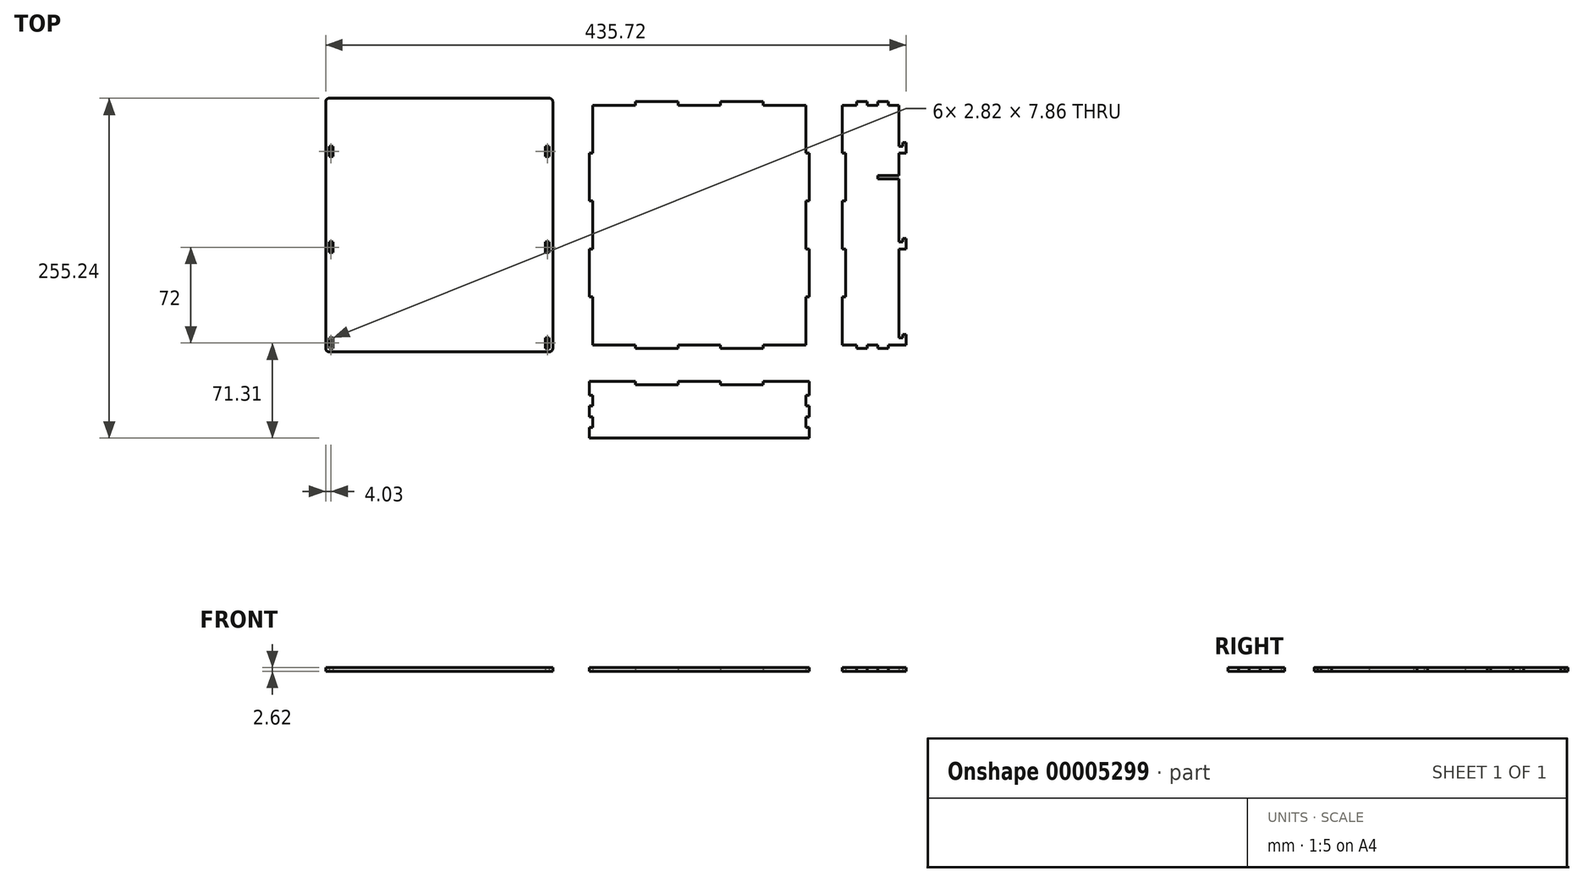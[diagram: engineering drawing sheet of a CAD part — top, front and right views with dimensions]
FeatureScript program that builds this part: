
annotation { "Feature Type Name" : "Feature", "Feature Type Description" : "" }
export const myFeature = defineFeature(function(context is Context, id is Id, definition is map)
    precondition{}
    {
        {
            assignVariable(context, id + "F0", {"name" : "MaterialThickness", "anyValue" : 2.62});
        }
        {
            var Q0;
            Q0=qCreatedBy(makeId("Top.planeOp"),FACE);
            var sketch = newSketch(context, id + "F1", { "sketchPlane" : qUnion([Q0])});
            skLineSegment(sketch, "E0", {"start": v(0, 0) * mm, "end": v(160, 0) * mm});
            skLineSegment(sketch, "E1", {"start": v(160, 0) * mm, "end": v(160, 180) * mm});
            skLineSegment(sketch, "E2", {"start": v(160, 180) * mm, "end": v(0, 180) * mm});
            skLineSegment(sketch, "E3", {"start": v(0, 180) * mm, "end": v(0, 0) * mm});
            skLineSegment(sketch, "E4", {"start": v(64, 182.62) * mm, "end": v(64, 180) * mm});
            skLineSegment(sketch, "E5", {"start": v(96, 180) * mm, "end": v(96, 182.62) * mm});
            skLineSegment(sketch, "E6", {"start": v(96, 182.62) * mm, "end": v(128, 182.62) * mm});
            skLineSegment(sketch, "E7", {"start": v(128, 182.62) * mm, "end": v(128, 180) * mm});
            skLineSegment(sketch, "E8", {"start": v(64, 182.62) * mm, "end": v(32, 182.62) * mm});
            skLineSegment(sketch, "E9", {"start": v(32, 182.62) * mm, "end": v(32, 180) * mm});
            skLineSegment(sketch, "E10", {"start": v(0, 90) * mm, "end": v(160, 90) * mm, "construction": true});
            skLineSegment(sketch, "E11.MirrorCS", {"start": v(64, -2.62) * mm, "end": v(64, 0) * mm});
            skLineSegment(sketch, "E12.MirrorCS", {"start": v(128, -2.62) * mm, "end": v(128, 0) * mm});
            skLineSegment(sketch, "E13.MirrorCS", {"start": v(32, -2.62) * mm, "end": v(32, 0) * mm});
            skLineSegment(sketch, "E14.MirrorCS", {"start": v(64, -2.62) * mm, "end": v(32, -2.62) * mm});
            skLineSegment(sketch, "E15.MirrorCS", {"start": v(96, 0) * mm, "end": v(96, -2.62) * mm});
            skLineSegment(sketch, "E16.MirrorCS", {"start": v(96, -2.62) * mm, "end": v(128, -2.62) * mm});
            skLineSegment(sketch, "E17", {"start": v(0, 144) * mm, "end": v(-2.62, 144) * mm});
            skLineSegment(sketch, "E18", {"start": v(-2.62, 144) * mm, "end": v(-2.62, 108) * mm});
            skLineSegment(sketch, "E19", {"start": v(-2.62, 108) * mm, "end": v(0, 108) * mm});
            skLineSegment(sketch, "E20", {"start": v(0, 72) * mm, "end": v(-2.62, 72) * mm});
            skLineSegment(sketch, "E21", {"start": v(-2.62, 72) * mm, "end": v(-2.62, 36) * mm});
            skLineSegment(sketch, "E22", {"start": v(-2.62, 36) * mm, "end": v(0, 36) * mm});
            skLineSegment(sketch, "E23", {"start": v(80, 180) * mm, "end": v(80, 0) * mm, "construction": true});
            skLineSegment(sketch, "E24.MirrorCS", {"start": v(162.62, 144) * mm, "end": v(162.62, 108) * mm});
            skLineSegment(sketch, "E25.MirrorCS", {"start": v(162.62, 108) * mm, "end": v(160, 108) * mm});
            skLineSegment(sketch, "E26.MirrorCS", {"start": v(162.62, 36) * mm, "end": v(160, 36) * mm});
            skLineSegment(sketch, "E27.MirrorCS", {"start": v(162.62, 72) * mm, "end": v(162.62, 36) * mm});
            skLineSegment(sketch, "E28.MirrorCS", {"start": v(160, 144) * mm, "end": v(162.62, 144) * mm});
            skLineSegment(sketch, "E29.MirrorCS", {"start": v(160, 72) * mm, "end": v(162.62, 72) * mm});
            skLineSegment(sketch, "E30", {"start": v(0, -30) * mm, "end": v(160, -30) * mm});
            skLineSegment(sketch, "E31", {"start": v(160, -30) * mm, "end": v(160, -70) * mm});
            skLineSegment(sketch, "E32", {"start": v(160, -70) * mm, "end": v(0, -70) * mm});
            skLineSegment(sketch, "E33", {"start": v(0, -70) * mm, "end": v(0, -30) * mm});
            skLineSegment(sketch, "E34", {"start": v(0, -30) * mm, "end": v(0, -27.38) * mm});
            skLineSegment(sketch, "E35", {"start": v(0, -27.38) * mm, "end": v(32, -27.38) * mm});
            skLineSegment(sketch, "E36", {"start": v(32, -27.38) * mm, "end": v(32, -30) * mm});
            skLineSegment(sketch, "E37", {"start": v(64, -30) * mm, "end": v(64, -27.38) * mm});
            skLineSegment(sketch, "E38", {"start": v(64, -27.38) * mm, "end": v(96, -27.38) * mm});
            skLineSegment(sketch, "E39", {"start": v(96, -27.38) * mm, "end": v(96, -30) * mm});
            skLineSegment(sketch, "E40", {"start": v(128, -30) * mm, "end": v(128, -27.38) * mm});
            skLineSegment(sketch, "E41", {"start": v(128, -27.38) * mm, "end": v(160, -27.38) * mm});
            skLineSegment(sketch, "E42", {"start": v(160, -27.38) * mm, "end": v(160, -30) * mm});
            skLineSegment(sketch, "E43", {"start": v(0, -27.38) * mm, "end": v(-2.62, -27.38) * mm});
            skLineSegment(sketch, "E44", {"start": v(-2.62, -27.38) * mm, "end": v(-2.62, -38) * mm});
            skLineSegment(sketch, "E45", {"start": v(-2.62, -38) * mm, "end": v(0, -38) * mm});
            skLineSegment(sketch, "E46", {"start": v(0, -46) * mm, "end": v(-2.62, -46) * mm});
            skLineSegment(sketch, "E47", {"start": v(-2.62, -46) * mm, "end": v(-2.62, -54) * mm});
            skLineSegment(sketch, "E48", {"start": v(-2.62, -54) * mm, "end": v(0, -54) * mm});
            skLineSegment(sketch, "E49", {"start": v(0, -70) * mm, "end": v(-2.62, -70) * mm});
            skLineSegment(sketch, "E50", {"start": v(-2.62, -70) * mm, "end": v(-2.62, -62) * mm});
            skLineSegment(sketch, "E51", {"start": v(-2.62, -62) * mm, "end": v(0, -62) * mm});
            skLineSegment(sketch, "E52", {"start": v(80, -30) * mm, "end": v(80, -70) * mm, "construction": true});
            skLineSegment(sketch, "E53.MirrorCS", {"start": v(160, -27.38) * mm, "end": v(162.62, -27.38) * mm});
            skLineSegment(sketch, "E54.MirrorCS", {"start": v(160, -70) * mm, "end": v(162.62, -70) * mm});
            skLineSegment(sketch, "E55.MirrorCS", {"start": v(160, -46) * mm, "end": v(162.62, -46) * mm});
            skLineSegment(sketch, "E56.MirrorCS", {"start": v(162.62, -38) * mm, "end": v(160, -38) * mm});
            skLineSegment(sketch, "E57.MirrorCS", {"start": v(162.62, -54) * mm, "end": v(160, -54) * mm});
            skLineSegment(sketch, "E58.MirrorCS", {"start": v(162.62, -62) * mm, "end": v(160, -62) * mm});
            skLineSegment(sketch, "E59.MirrorCS", {"start": v(162.62, -27.38) * mm, "end": v(162.62, -38) * mm});
            skLineSegment(sketch, "E60.MirrorCS", {"start": v(162.62, -46) * mm, "end": v(162.62, -54) * mm});
            skLineSegment(sketch, "E61.MirrorCS", {"start": v(162.62, -70) * mm, "end": v(162.62, -62) * mm});
            skLineSegment(sketch, "E62", {"start": v(190, 0) * mm, "end": v(190, 180) * mm});
            skLineSegment(sketch, "E63", {"start": v(190, 180) * mm, "end": v(230, 180) * mm});
            skLineSegment(sketch, "E64", {"start": v(230, 180) * mm, "end": v(230, 0) * mm});
            skLineSegment(sketch, "E65", {"start": v(230, 0) * mm, "end": v(190, 0) * mm});
            skLineSegment(sketch, "E66", {"start": v(198, 0) * mm, "end": v(198, -2.62) * mm});
            skLineSegment(sketch, "E67", {"start": v(198, -2.62) * mm, "end": v(206, -2.62) * mm});
            skLineSegment(sketch, "E68", {"start": v(206, -2.62) * mm, "end": v(206, 0) * mm});
            skLineSegment(sketch, "E69", {"start": v(214, 0) * mm, "end": v(214, -2.62) * mm});
            skLineSegment(sketch, "E70", {"start": v(214, -2.62) * mm, "end": v(222, -2.62) * mm});
            skLineSegment(sketch, "E71", {"start": v(222, -2.62) * mm, "end": v(222, 0) * mm});
            skLineSegment(sketch, "E72", {"start": v(190, 0) * mm, "end": v(187.38, 0) * mm});
            skLineSegment(sketch, "E73", {"start": v(187.38, 0) * mm, "end": v(187.38, 36) * mm});
            skLineSegment(sketch, "E74", {"start": v(187.38, 36) * mm, "end": v(190, 36) * mm});
            skLineSegment(sketch, "E75", {"start": v(190, 72) * mm, "end": v(187.38, 72) * mm});
            skLineSegment(sketch, "E76", {"start": v(187.38, 72) * mm, "end": v(187.38, 108) * mm});
            skLineSegment(sketch, "E77", {"start": v(187.38, 108) * mm, "end": v(190, 108) * mm});
            skLineSegment(sketch, "E78", {"start": v(190, 144) * mm, "end": v(187.38, 144) * mm});
            skLineSegment(sketch, "E79", {"start": v(187.38, 144) * mm, "end": v(187.38, 180) * mm});
            skLineSegment(sketch, "E80", {"start": v(187.38, 180) * mm, "end": v(190, 180) * mm});
            skLineSegment(sketch, "E81", {"start": v(190, 90) * mm, "end": v(230, 90) * mm, "construction": true});
            skLineSegment(sketch, "E82.MirrorCS", {"start": v(214, 180) * mm, "end": v(214, 182.62) * mm});
            skLineSegment(sketch, "E83.MirrorCS", {"start": v(222, 182.62) * mm, "end": v(222, 180) * mm});
            skLineSegment(sketch, "E84.MirrorCS", {"start": v(206, 182.62) * mm, "end": v(206, 180) * mm});
            skLineSegment(sketch, "E85.MirrorCS", {"start": v(198, 180) * mm, "end": v(198, 182.62) * mm});
            skLineSegment(sketch, "E86.MirrorCS", {"start": v(198, 182.62) * mm, "end": v(206, 182.62) * mm});
            skLineSegment(sketch, "E87.MirrorCS", {"start": v(214, 182.62) * mm, "end": v(222, 182.62) * mm});
            skLineSegment(sketch, "E88", {"start": v(230, 0) * mm, "end": v(235.24, 0) * mm});
            skLineSegment(sketch, "E89", {"start": v(235.24, 0) * mm, "end": v(235.24, 7.86) * mm});
            skLineSegment(sketch, "E90", {"start": v(235.24, 7.86) * mm, "end": v(232.62, 7.86) * mm});
            skLineSegment(sketch, "E91", {"start": v(232.62, 7.86) * mm, "end": v(232.62, 5.24) * mm});
            skLineSegment(sketch, "E92", {"start": v(232.62, 5.24) * mm, "end": v(230, 5.24) * mm});
            skLineSegment(sketch, "E93", {"start": v(230, 72) * mm, "end": v(235.24, 72) * mm});
            skLineSegment(sketch, "E94", {"start": v(235.24, 72) * mm, "end": v(235.24, 79.86) * mm});
            skLineSegment(sketch, "E95", {"start": v(235.24, 79.86) * mm, "end": v(232.62, 79.86) * mm});
            skLineSegment(sketch, "E96", {"start": v(232.62, 79.86) * mm, "end": v(232.62, 77.24) * mm});
            skLineSegment(sketch, "E97", {"start": v(232.62, 77.24) * mm, "end": v(230, 77.24) * mm});
            skLineSegment(sketch, "E98", {"start": v(230, 144) * mm, "end": v(235.24, 144) * mm});
            skLineSegment(sketch, "E99", {"start": v(235.24, 144) * mm, "end": v(235.24, 151.86) * mm});
            skLineSegment(sketch, "E100", {"start": v(235.24, 151.86) * mm, "end": v(232.62, 151.86) * mm});
            skLineSegment(sketch, "E101", {"start": v(232.62, 151.86) * mm, "end": v(232.62, 149.24) * mm});
            skLineSegment(sketch, "E102", {"start": v(232.62, 149.24) * mm, "end": v(230, 149.24) * mm});
            skLineSegment(sketch, "E103", {"start": v(-30, -5.24) * mm, "end": v(-30, 185.24) * mm});
            skLineSegment(sketch, "E104", {"start": v(-30, 185.24) * mm, "end": v(-200.48, 185.24) * mm});
            skLineSegment(sketch, "E105", {"start": v(-200.48, 185.24) * mm, "end": v(-200.48, -5.24) * mm});
            skLineSegment(sketch, "E106", {"start": v(-200.48, -5.24) * mm, "end": v(-30, -5.24) * mm});
            skLineSegment(sketch, "E107", {"start": v(-32.62, 5.24) * mm, "end": v(-35.44, 5.24) * mm});
            skLineSegment(sketch, "E108", {"start": v(-35.44, 5.24) * mm, "end": v(-35.44, -2.62) * mm});
            skLineSegment(sketch, "E109", {"start": v(-35.44, -2.62) * mm, "end": v(-32.62, -2.62) * mm});
            skLineSegment(sketch, "E110", {"start": v(-32.62, -2.62) * mm, "end": v(-32.62, 5.24) * mm});
            skLineSegment(sketch, "E111", {"start": v(-32.62, 77.24) * mm, "end": v(-35.44, 77.24) * mm});
            skLineSegment(sketch, "E112", {"start": v(-35.44, 77.24) * mm, "end": v(-35.44, 69.38) * mm});
            skLineSegment(sketch, "E113", {"start": v(-35.44, 69.38) * mm, "end": v(-32.62, 69.38) * mm});
            skLineSegment(sketch, "E114", {"start": v(-32.62, 69.38) * mm, "end": v(-32.62, 77.24) * mm});
            skLineSegment(sketch, "E115", {"start": v(-115.24, -5.24) * mm, "end": v(-115.24, 185.24) * mm, "construction": true});
            skLineSegment(sketch, "E116", {"start": v(-32.62, 149.24) * mm, "end": v(-35.44, 149.24) * mm});
            skLineSegment(sketch, "E117", {"start": v(-35.44, 149.24) * mm, "end": v(-35.44, 141.38) * mm});
            skLineSegment(sketch, "E118", {"start": v(-35.44, 141.38) * mm, "end": v(-32.62, 141.38) * mm});
            skLineSegment(sketch, "E119", {"start": v(-32.62, 141.38) * mm, "end": v(-32.62, 149.24) * mm});
            skLineSegment(sketch, "E120.MirrorCS", {"start": v(-195.04, 69.38) * mm, "end": v(-197.86, 69.38) * mm});
            skLineSegment(sketch, "E121.MirrorCS", {"start": v(-197.86, 69.38) * mm, "end": v(-197.86, 77.24) * mm});
            skLineSegment(sketch, "E122.MirrorCS", {"start": v(-197.86, 5.24) * mm, "end": v(-195.04, 5.24) * mm});
            skLineSegment(sketch, "E123.MirrorCS", {"start": v(-195.04, 77.24) * mm, "end": v(-195.04, 69.38) * mm});
            skLineSegment(sketch, "E124.MirrorCS", {"start": v(-195.04, -2.62) * mm, "end": v(-197.86, -2.62) * mm});
            skLineSegment(sketch, "E125.MirrorCS", {"start": v(-195.04, 5.24) * mm, "end": v(-195.04, -2.62) * mm});
            skLineSegment(sketch, "E126.MirrorCS", {"start": v(-197.86, 77.24) * mm, "end": v(-195.04, 77.24) * mm});
            skLineSegment(sketch, "E127.MirrorCS", {"start": v(-197.86, 149.24) * mm, "end": v(-195.04, 149.24) * mm});
            skLineSegment(sketch, "E128.MirrorCS", {"start": v(-197.86, -2.62) * mm, "end": v(-197.86, 5.24) * mm});
            skLineSegment(sketch, "E129.MirrorCS", {"start": v(-195.04, 149.24) * mm, "end": v(-195.04, 141.38) * mm});
            skLineSegment(sketch, "E130.MirrorCS", {"start": v(-197.86, 141.38) * mm, "end": v(-197.86, 149.24) * mm});
            skLineSegment(sketch, "E131.MirrorCS", {"start": v(-195.04, 141.38) * mm, "end": v(-197.86, 141.38) * mm});
            skLineSegment(sketch, "E132", {"start": v(230, 127.31) * mm, "end": v(214, 127.31) * mm});
            skLineSegment(sketch, "E133", {"start": v(214, 127.3) * mm, "end": v(214, 124.7) * mm});
            skLineSegment(sketch, "E134", {"start": v(214, 124.7) * mm, "end": v(230, 124.69) * mm});
            skLineSegment(sketch, "E135", {"start": v(214, 126) * mm, "end": v(230, 126) * mm, "construction": true});
            skPoint(sketch, "E136", {"position": v(187.38, 18) * mm});
            skSolve(sketch);
        }
        {
            var Q0;
            Q0=makeQuery(id+"F1.imprint","IMPRINT",FACE,{"disambiguationData":[TD([[makeQuery(id+"F1.imprint","IMPRINT",EDGE,{"derivedFrom":sQuery(id+"F1.wireOp",EDGE,"E103")}),1.0]])]});
            var Q1;
            {var subQ15=sQuery(id+"F1.wireOp",EDGE,"E32");Q1=makeQuery(id+"F1.imprint","IMPRINT",FACE,{"disambiguationData":[TD([[makeQuery(id+"F1.imprint","IMPRINT",EDGE,{"derivedFrom":subQ15}),-1.0]])]});}
            var Q2;
            {var subQ0=sQuery(id+"F1.wireOp",EDGE,"E34");Q2=makeQuery(id+"F1.imprint","IMPRINT",FACE,{"disambiguationData":[TD([[makeQuery(id+"F1.imprint","IMPRINT",EDGE,{"derivedFrom":subQ0}),-1.0]])]});}
            var Q3;
            {var subQ5=sQuery(id+"F1.wireOp",EDGE,"E62");var subQ7=makeQuery(id+"F1.imprint","INTERSECT",VERTEX,{"derivedFrom":[subQ5,sQuery(id+"F1.wireOp",EDGE,"E74")]});Q3=makeQuery(id+"F1.imprint","IMPRINT",FACE,{"disambiguationData":[TD([[makeQuery(id+"F1.imprint","IMPRINT",EDGE,{"disambiguationData":[TD([[subQ7,-1.0]])],"derivedFrom":subQ5}),-1.0]])]});}
            var Q4;
            {var subQ0=sQuery(id+"F1.wireOp",EDGE,"E69");Q4=makeQuery(id+"F1.imprint","IMPRINT",FACE,{"disambiguationData":[TD([[makeQuery(id+"F1.imprint","IMPRINT",EDGE,{"derivedFrom":subQ0}),1.0]])]});}
            var Q5;
            {var subQ2=sQuery(id+"F1.wireOp",EDGE,"E40");Q5=makeQuery(id+"F1.imprint","IMPRINT",FACE,{"disambiguationData":[TD([[makeQuery(id+"F1.imprint","IMPRINT",EDGE,{"derivedFrom":subQ2}),-1.0]])]});}
            var Q6;
            {var subQ0=sQuery(id+"F1.wireOp",EDGE,"E66");Q6=makeQuery(id+"F1.imprint","IMPRINT",FACE,{"disambiguationData":[TD([[makeQuery(id+"F1.imprint","IMPRINT",EDGE,{"derivedFrom":subQ0}),1.0]])]});}
            var Q7;
            {var subQ2=sQuery(id+"F1.wireOp",EDGE,"E78");Q7=makeQuery(id+"F1.imprint","IMPRINT",FACE,{"disambiguationData":[TD([[makeQuery(id+"F1.imprint","IMPRINT",EDGE,{"derivedFrom":subQ2}),-1.0]])]});}
            var Q8;
            {var subQ0=sQuery(id+"F1.wireOp",EDGE,"E72");Q8=makeQuery(id+"F1.imprint","IMPRINT",FACE,{"disambiguationData":[TD([[makeQuery(id+"F1.imprint","IMPRINT",EDGE,{"derivedFrom":subQ0}),-1.0]])]});}
            var Q9;
            {var subQ0=sQuery(id+"F1.wireOp",EDGE,"E84.MirrorCS");Q9=makeQuery(id+"F1.imprint","IMPRINT",FACE,{"disambiguationData":[TD([[makeQuery(id+"F1.imprint","IMPRINT",EDGE,{"derivedFrom":subQ0}),-1.0]])]});}
            var Q10;
            {var subQ0=sQuery(id+"F1.wireOp",EDGE,"E34");Q10=makeQuery(id+"F1.imprint","IMPRINT",FACE,{"disambiguationData":[TD([[makeQuery(id+"F1.imprint","IMPRINT",EDGE,{"derivedFrom":subQ0}),1.0]])]});}
            var Q11;
            {var subQ0=sQuery(id+"F1.wireOp",EDGE,"E11.MirrorCS");Q11=makeQuery(id+"F1.imprint","IMPRINT",FACE,{"disambiguationData":[TD([[makeQuery(id+"F1.imprint","IMPRINT",EDGE,{"derivedFrom":subQ0}),1.0]])]});}
            var Q12;
            {var subQ0=sQuery(id+"F1.wireOp",EDGE,"E12.MirrorCS");Q12=makeQuery(id+"F1.imprint","IMPRINT",FACE,{"disambiguationData":[TD([[makeQuery(id+"F1.imprint","IMPRINT",EDGE,{"derivedFrom":subQ0}),1.0]])]});}
            var Q13;
            {var subQ0=sQuery(id+"F1.wireOp",EDGE,"E26.MirrorCS");Q13=makeQuery(id+"F1.imprint","IMPRINT",FACE,{"disambiguationData":[TD([[makeQuery(id+"F1.imprint","IMPRINT",EDGE,{"derivedFrom":subQ0}),-1.0]])]});}
            var Q14;
            Q14=makeQuery(id+"F1.imprint","IMPRINT",FACE,{"disambiguationData":[TD([[makeQuery(id+"F1.imprint","IMPRINT",EDGE,{"derivedFrom":sQuery(id+"F1.wireOp",EDGE,"E24.MirrorCS")}),-1.0]])]});
            var Q15;
            {var subQ0=sQuery(id+"F1.wireOp",EDGE,"E5");Q15=makeQuery(id+"F1.imprint","IMPRINT",FACE,{"disambiguationData":[TD([[makeQuery(id+"F1.imprint","IMPRINT",EDGE,{"derivedFrom":subQ0}),-1.0]])]});}
            var Q16;
            {var subQ0=sQuery(id+"F1.wireOp",EDGE,"E4");Q16=makeQuery(id+"F1.imprint","IMPRINT",FACE,{"disambiguationData":[TD([[makeQuery(id+"F1.imprint","IMPRINT",EDGE,{"derivedFrom":subQ0}),-1.0]])]});}
            var Q17;
            {var subQ0=sQuery(id+"F1.wireOp",EDGE,"E17");Q17=makeQuery(id+"F1.imprint","IMPRINT",FACE,{"disambiguationData":[TD([[makeQuery(id+"F1.imprint","IMPRINT",EDGE,{"derivedFrom":subQ0}),1.0]])]});}
            var Q18;
            {var subQ0=sQuery(id+"F1.wireOp",EDGE,"E20");Q18=makeQuery(id+"F1.imprint","IMPRINT",FACE,{"disambiguationData":[TD([[makeQuery(id+"F1.imprint","IMPRINT",EDGE,{"derivedFrom":subQ0}),1.0]])]});}
            var Q19;
            {var subQ0=sQuery(id+"F1.wireOp",EDGE,"E37");Q19=makeQuery(id+"F1.imprint","IMPRINT",FACE,{"disambiguationData":[TD([[makeQuery(id+"F1.imprint","IMPRINT",EDGE,{"derivedFrom":subQ0}),-1.0]])]});}
            var Q20;
            {var subQ0=sQuery(id+"F1.wireOp",EDGE,"E55.MirrorCS");Q20=makeQuery(id+"F1.imprint","IMPRINT",FACE,{"disambiguationData":[TD([[makeQuery(id+"F1.imprint","IMPRINT",EDGE,{"derivedFrom":subQ0}),-1.0]])]});}
            var Q21;
            {var subQ0=sQuery(id+"F1.wireOp",EDGE,"E54.MirrorCS");Q21=makeQuery(id+"F1.imprint","IMPRINT",FACE,{"disambiguationData":[TD([[makeQuery(id+"F1.imprint","IMPRINT",EDGE,{"derivedFrom":subQ0}),1.0]])]});}
            var Q22;
            {var subQ0=sQuery(id+"F1.wireOp",EDGE,"E49");Q22=makeQuery(id+"F1.imprint","IMPRINT",FACE,{"disambiguationData":[TD([[makeQuery(id+"F1.imprint","IMPRINT",EDGE,{"derivedFrom":subQ0}),-1.0]])]});}
            var Q23;
            {var subQ0=sQuery(id+"F1.wireOp",EDGE,"E46");Q23=makeQuery(id+"F1.imprint","IMPRINT",FACE,{"disambiguationData":[TD([[makeQuery(id+"F1.imprint","IMPRINT",EDGE,{"derivedFrom":subQ0}),1.0]])]});}
            var Q24;
            {var subQ0=sQuery(id+"F1.wireOp",EDGE,"E82.MirrorCS");Q24=makeQuery(id+"F1.imprint","IMPRINT",FACE,{"disambiguationData":[TD([[makeQuery(id+"F1.imprint","IMPRINT",EDGE,{"derivedFrom":subQ0}),-1.0]])]});}
            var Q25;
            {var subQ3=sQuery(id+"F1.wireOp",EDGE,"E3");var subQ4=sQuery(id+"F1.wireOp",EDGE,"E0");var subQ5=makeQuery(id+"F1.imprint","INTERSECT",VERTEX,{"derivedFrom":[subQ4,subQ3]});Q25=makeQuery(id+"F1.imprint","IMPRINT",FACE,{"disambiguationData":[TD([[makeQuery(id+"F1.imprint","IMPRINT",EDGE,{"disambiguationData":[TD([[subQ5,-1.0]])],"derivedFrom":subQ4}),1.0]])]});}
            var Q26;
            {var subQ0=sQuery(id+"F1.wireOp",EDGE,"E42");Q26=makeQuery(id+"F1.imprint","IMPRINT",FACE,{"disambiguationData":[TD([[makeQuery(id+"F1.imprint","IMPRINT",EDGE,{"derivedFrom":subQ0}),1.0]])]});}
            var Q27;
            {var subQ0=sQuery(id+"F1.wireOp",EDGE,"E88");Q27=makeQuery(id+"F1.imprint","IMPRINT",FACE,{"disambiguationData":[TD([[makeQuery(id+"F1.imprint","IMPRINT",EDGE,{"derivedFrom":subQ0}),1.0]])]});}
            var Q28;
            {var subQ0=sQuery(id+"F1.wireOp",EDGE,"E75");Q28=makeQuery(id+"F1.imprint","IMPRINT",FACE,{"disambiguationData":[TD([[makeQuery(id+"F1.imprint","IMPRINT",EDGE,{"derivedFrom":subQ0}),-1.0]])]});}
            var Q29;
            {var subQ0=sQuery(id+"F1.wireOp",EDGE,"E98");Q29=makeQuery(id+"F1.imprint","IMPRINT",FACE,{"disambiguationData":[TD([[makeQuery(id+"F1.imprint","IMPRINT",EDGE,{"derivedFrom":subQ0}),1.0]])]});}
            var Q30;
            {var subQ0=sQuery(id+"F1.wireOp",EDGE,"E93");Q30=makeQuery(id+"F1.imprint","IMPRINT",FACE,{"disambiguationData":[TD([[makeQuery(id+"F1.imprint","IMPRINT",EDGE,{"derivedFrom":subQ0}),1.0]])]});}
            extrude(context, id + "F2", {"entities" : qUnion([Q0, Q1, Q2, Q3, Q4, Q5, Q6, Q7, Q8, Q9, Q10, Q11, Q12, Q13, Q14, Q15, Q16, Q17, Q18, Q19, Q20, Q21, Q22, Q23, Q24, Q25, Q26, Q27, Q28, Q29, Q30]), "depth" : (getVariable(context, 'MaterialThickness')) * mm});
        }
        {
            var Q0;
            Q0=makeQuery(id+"F2.opExtrude","SWEPT_EDGE",EDGE,{"disambiguationData":[OSD([sQuery(id+"F1.wireOp",EDGE,"E103"),sQuery(id+"F1.wireOp",EDGE,"E106")])]});
            var Q1;
            Q1=makeQuery(id+"F2.opExtrude","SWEPT_EDGE",EDGE,{"disambiguationData":[OSD([sQuery(id+"F1.wireOp",EDGE,"E105"),sQuery(id+"F1.wireOp",EDGE,"E106")])]});
            var Q2;
            Q2=makeQuery(id+"F2.opExtrude","SWEPT_EDGE",EDGE,{"disambiguationData":[OSD([sQuery(id+"F1.wireOp",EDGE,"E104"),sQuery(id+"F1.wireOp",EDGE,"E105")])]});
            var Q3;
            Q3=makeQuery(id+"F2.opExtrude","SWEPT_EDGE",EDGE,{"disambiguationData":[OSD([sQuery(id+"F1.wireOp",EDGE,"E103"),sQuery(id+"F1.wireOp",EDGE,"E104")])]});
            fillet(context, id + "F3", {"entities" : qUnion([Q0, Q1, Q2, Q3]), "radius" : (getVariable(context, 'MaterialThickness')) * mm, "tangentPropagation" : true, "allowEdgeOverflow" : false});
        }
    });
